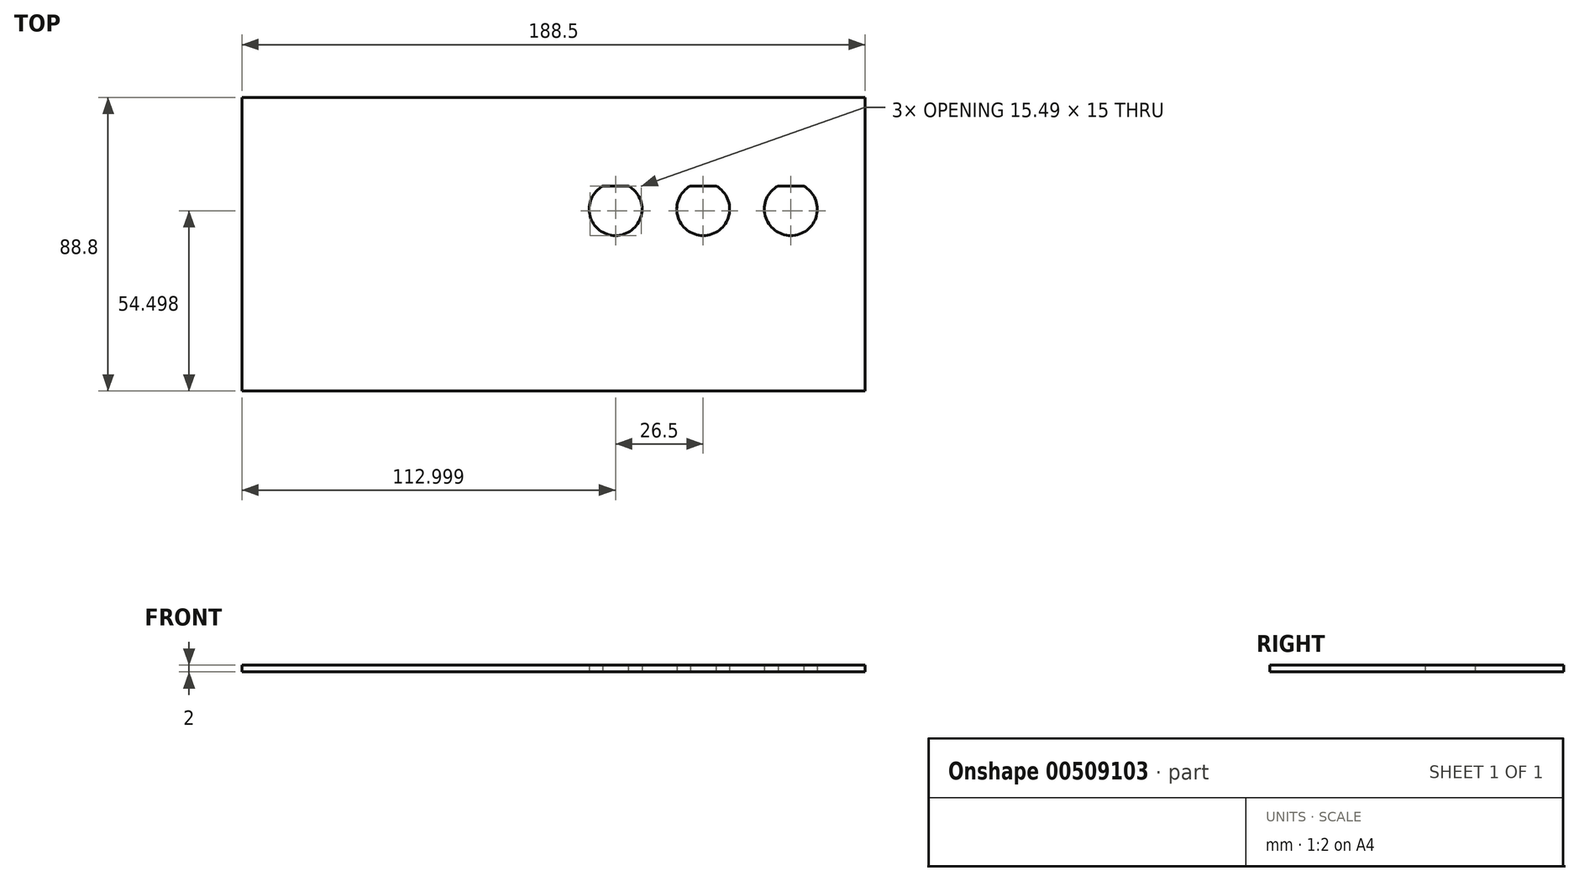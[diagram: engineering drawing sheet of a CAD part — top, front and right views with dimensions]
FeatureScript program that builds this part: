
annotation { "Feature Type Name" : "Feature", "Feature Type Description" : "" }
export const myFeature = defineFeature(function(context is Context, id is Id, definition is map)
    precondition{}
    {
        {
            var Q0;
            Q0=qCreatedBy(makeId("Top.planeOp"),FACE);
            var sketch = newSketch(context, id + "F0", { "sketchPlane" : qUnion([Q0])});
            skLineSegment(sketch, "E0.bottom", {"start": v(-103.11, 36.24) * mm, "end": v(85.39, 36.24) * mm});
            skLineSegment(sketch, "E0.top", {"start": v(-103.11, -52.56) * mm, "end": v(85.39, -52.56) * mm});
            skLineSegment(sketch, "E0.left", {"start": v(-103.11, 36.24) * mm, "end": v(-103.11, -52.56) * mm});
            skLineSegment(sketch, "E0.right", {"start": v(85.39, 36.24) * mm, "end": v(85.39, -52.56) * mm});
            skArc(sketch, "E1", {"start": v(6.02, 9.44) * mm, "mid": v(9.89, -5.56) * mm, "end": v(13.76, 9.44) * mm});
            skArc(sketch, "E2", {"start": v(32.52, 9.44) * mm, "mid": v(36.39, -5.56) * mm, "end": v(40.26, 9.44) * mm});
            skArc(sketch, "E3", {"start": v(59.02, 9.44) * mm, "mid": v(62.89, -5.56) * mm, "end": v(66.76, 9.44) * mm});
            skLineSegment(sketch, "E4", {"start": v(6.02, 9.44) * mm, "end": v(13.76, 9.44) * mm});
            skLineSegment(sketch, "E5.trimOffspring", {"start": v(32.52, 9.44) * mm, "end": v(40.26, 9.44) * mm});
            skLineSegment(sketch, "E6.trimOffspring", {"start": v(59.02, 9.44) * mm, "end": v(66.76, 9.44) * mm});
            skSolve(sketch);
        }
        {
            var Q0;
            Q0=makeQuery(id+"F0.imprint","IMPRINT",FACE,{"disambiguationData":[TD([[makeQuery(id+"F0.imprint","IMPRINT",EDGE,{"derivedFrom":sQuery(id+"F0.wireOp",EDGE,"E0.bottom")}),-1.0]])]});
            extrude(context, id + "F1", {"entities" : qUnion([Q0]), "depth" : 2 * mm});
        }
    });
